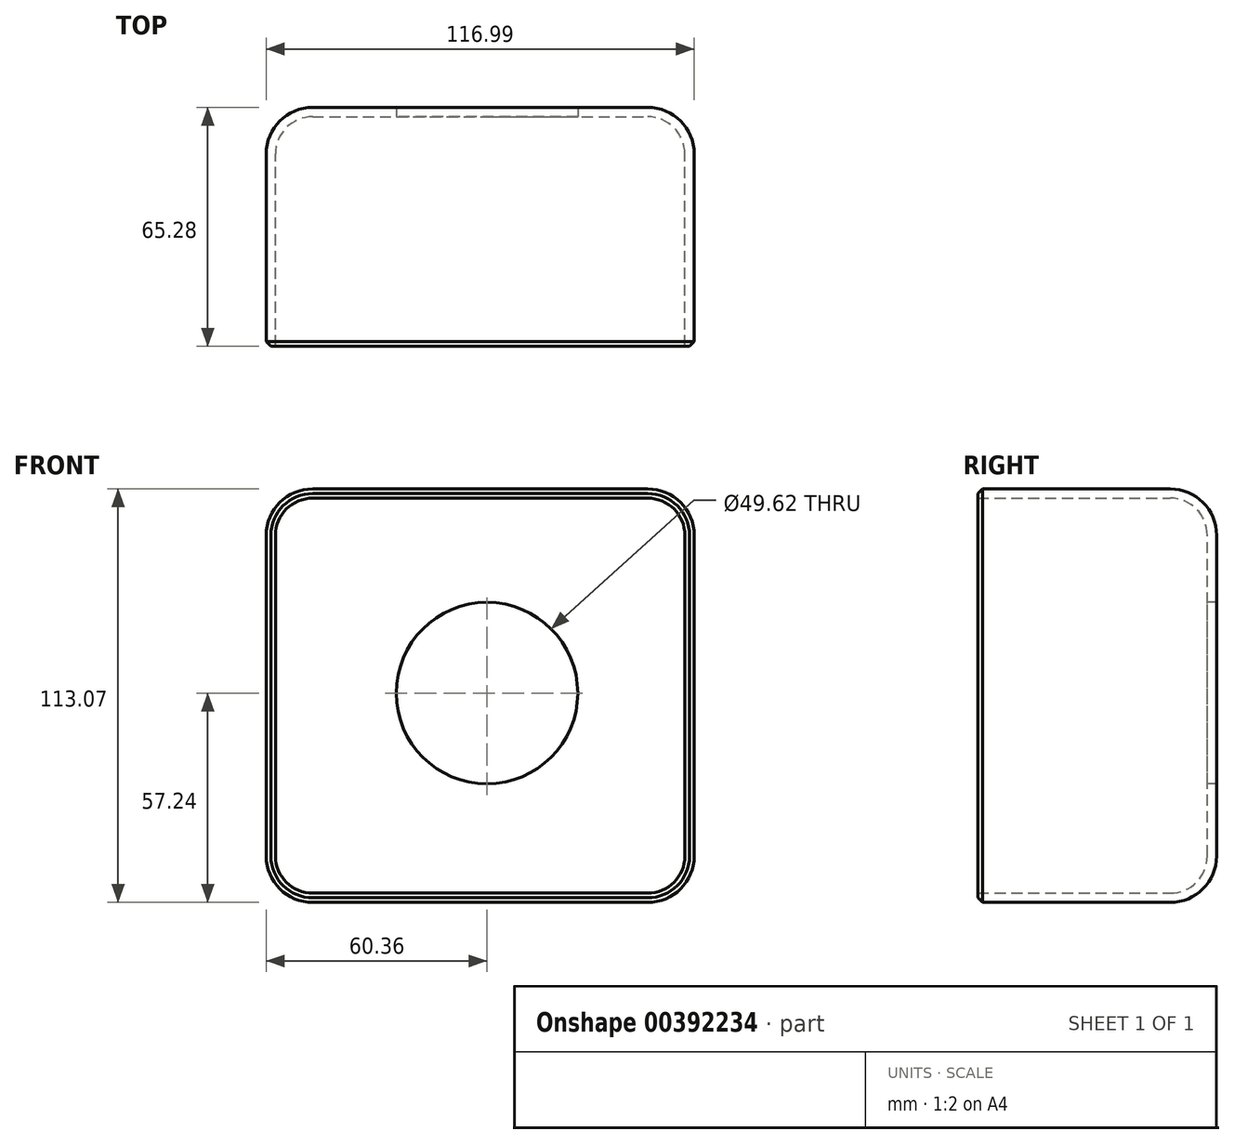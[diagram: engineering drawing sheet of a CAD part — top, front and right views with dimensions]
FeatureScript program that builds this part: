
annotation { "Feature Type Name" : "Feature", "Feature Type Description" : "" }
export const myFeature = defineFeature(function(context is Context, id is Id, definition is map)
    precondition{}
    {
        {
            var Q0;
            Q0=qCreatedBy(makeId("Front.planeOp"),FACE);
            var sketch = newSketch(context, id + "F0", { "sketchPlane" : qUnion([Q0])});
            skLineSegment(sketch, "E0.bottom", {"start": v(-60.36, 55.83) * mm, "end": v(56.63, 55.83) * mm});
            skLineSegment(sketch, "E0.top", {"start": v(-60.36, -57.24) * mm, "end": v(56.63, -57.24) * mm});
            skLineSegment(sketch, "E0.left", {"start": v(-60.36, 55.83) * mm, "end": v(-60.36, -57.24) * mm});
            skLineSegment(sketch, "E0.right", {"start": v(56.63, 55.83) * mm, "end": v(56.63, -57.24) * mm});
            skSolve(sketch);
        }
        {
            var Q0;
            Q0=makeQuery(id+"F0.imprint","IMPRINT",FACE,{"disambiguationData":[TD([[makeQuery(id+"F0.imprint","IMPRINT",EDGE,{"derivedFrom":sQuery(id+"F0.wireOp",EDGE,"E0.bottom")}),-1.0]])]});
            extrude(context, id + "F1", {"entities" : qUnion([Q0]), "depth" : 65.28 * mm});
        }
        {
            var Q0;
            Q0=makeQuery(id+"F1.opExtrude","CAP_EDGE",EDGE,{"disambiguationData":[OSD([sQuery(id+"F0.wireOp",EDGE,"E0.bottom")])],"isStart":true});
            var Q1;
            Q1=makeQuery(id+"F1.opExtrude","SWEPT_EDGE",EDGE,{"disambiguationData":[OSD([sQuery(id+"F0.wireOp",EDGE,"E0.bottom"),sQuery(id+"F0.wireOp",EDGE,"E0.right")])]});
            var Q2;
            Q2=makeQuery(id+"F1.opExtrude","CAP_EDGE",EDGE,{"disambiguationData":[OSD([sQuery(id+"F0.wireOp",EDGE,"E0.right")])],"isStart":true});
            var Q3;
            Q3=makeQuery(id+"F1.opExtrude","SWEPT_EDGE",EDGE,{"disambiguationData":[OSD([sQuery(id+"F0.wireOp",EDGE,"E0.top"),sQuery(id+"F0.wireOp",EDGE,"E0.right")])]});
            var Q4;
            Q4=makeQuery(id+"F1.opExtrude","CAP_EDGE",EDGE,{"disambiguationData":[OSD([sQuery(id+"F0.wireOp",EDGE,"E0.top")])],"isStart":true});
            var Q5;
            Q5=makeQuery(id+"F1.opExtrude","SWEPT_EDGE",EDGE,{"disambiguationData":[OSD([sQuery(id+"F0.wireOp",EDGE,"E0.top"),sQuery(id+"F0.wireOp",EDGE,"E0.left")])]});
            var Q6;
            Q6=makeQuery(id+"F1.opExtrude","CAP_EDGE",EDGE,{"disambiguationData":[OSD([sQuery(id+"F0.wireOp",EDGE,"E0.left")])],"isStart":true});
            var Q7;
            Q7=makeQuery(id+"F1.opExtrude","SWEPT_EDGE",EDGE,{"disambiguationData":[OSD([sQuery(id+"F0.wireOp",EDGE,"E0.bottom"),sQuery(id+"F0.wireOp",EDGE,"E0.left")])]});
            fillet(context, id + "F2", {"entities" : qUnion([Q0, Q1, Q2, Q3, Q4, Q5, Q6, Q7]), "radius" : 12.7 * mm, "tangentPropagation" : true, "allowEdgeOverflow" : false});
        }
        {
            var Q0;
            Q0=makeQuery(id+"F1.opExtrude","CAP_FACE",FACE,{"disambiguationData":[OSD([sQuery(id+"F0.wireOp",EDGE,"E0.bottom"),sQuery(id+"F0.wireOp",EDGE,"E0.top"),sQuery(id+"F0.wireOp",EDGE,"E0.left"),sQuery(id+"F0.wireOp",EDGE,"E0.right")])],"isStart":false});
            shell(context, id + "F3", {"entities" : qUnion([Q0]), "thickness" : 2.54 * mm});
        }
        {
            var Q0;
            Q0=makeQuery(id+"F3.opShell","OFFSET_FACE",FACE,{"disambiguationData":[OSD([sQuery(id+"F0.wireOp",EDGE,"E0.bottom"),sQuery(id+"F0.wireOp",EDGE,"E0.top"),sQuery(id+"F0.wireOp",EDGE,"E0.left"),sQuery(id+"F0.wireOp",EDGE,"E0.right")])]});
            var sketch = newSketch(context, id + "F4", { "sketchPlane" : qUnion([Q0])});
            skCircle(sketch, "E1", {"center": v(0, 0) * mm, "radius": 24.81 * mm});
            skSolve(sketch);
        }
        {
            var Q0;
            Q0=makeQuery(id+"F4.imprint","IMPRINT",FACE,{"disambiguationData":[TD([[makeQuery(id+"F4.imprint","IMPRINT",EDGE,{"derivedFrom":sQuery(id+"F4.wireOp",EDGE,"E1")}),1.0]])]});
            var Q1;
            Q1=sQuery(id+"F4.wireOp",EDGE,"E1");
            extrude(context, id + "F5", {"entities" : qUnion([Q0]), "operationType" : NewBodyOperationType.REMOVE, "surfaceEntities" : qUnion([Q1]), "oppositeDirection" : true, "depth" : 64 * mm});
        }
        {
            var Q0;
            Q0=makeQuery(id+"F1.opExtrude","CAP_EDGE",EDGE,{"disambiguationData":[OSD([sQuery(id+"F0.wireOp",EDGE,"E0.bottom")])],"isStart":false});
            chamfer(context, id + "F6", {"entities" : qUnion([Q0]), "width" : 1.27 * mm, "tangentPropagation" : true});
        }
    });
